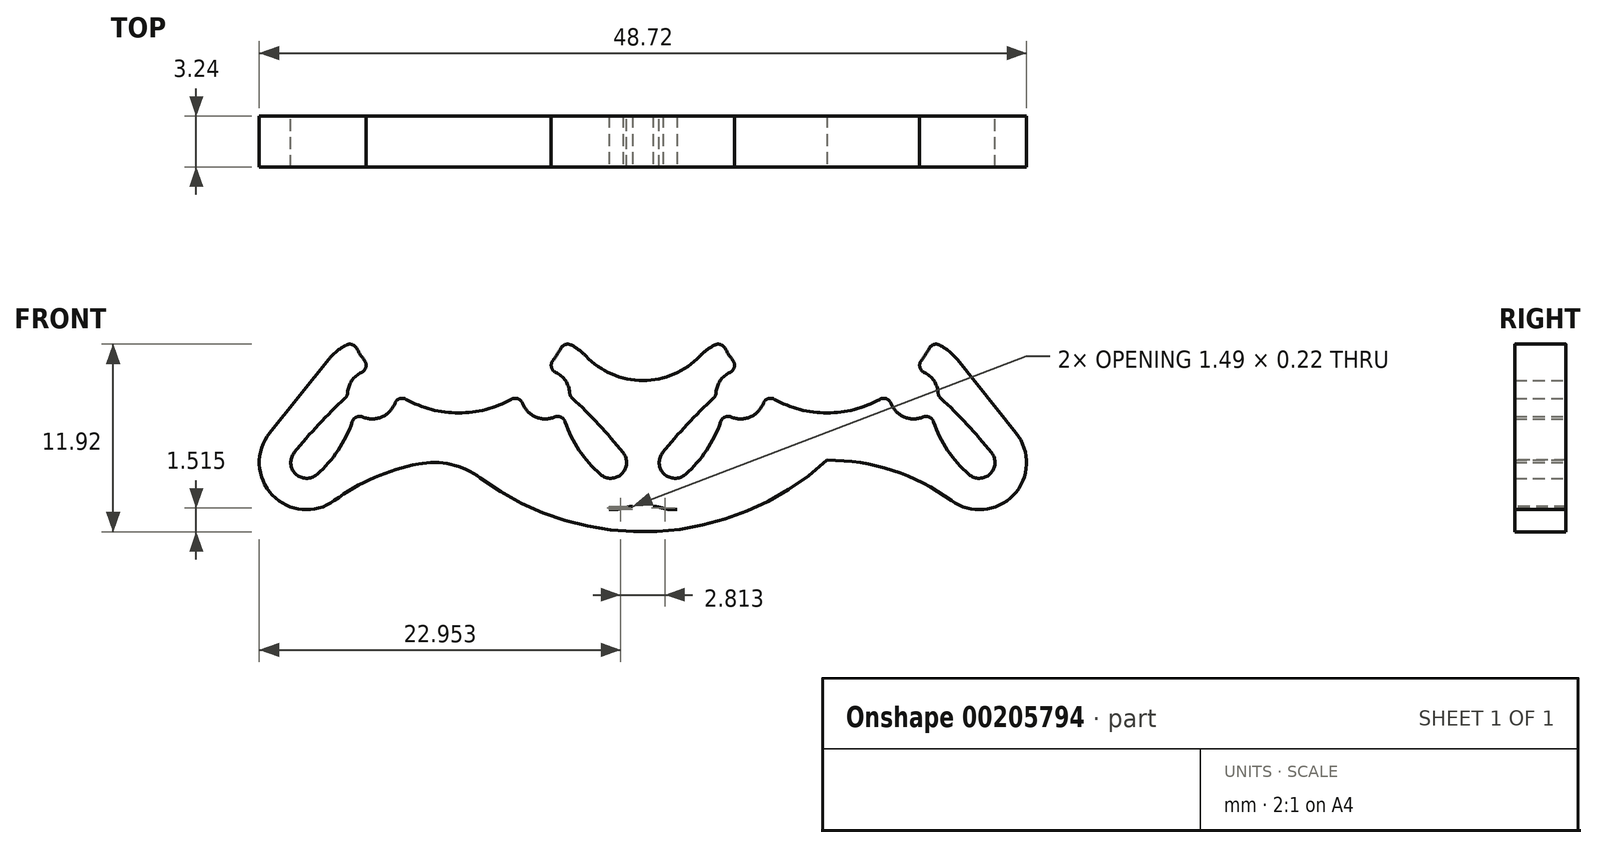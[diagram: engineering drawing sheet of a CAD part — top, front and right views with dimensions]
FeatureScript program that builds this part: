
annotation { "Feature Type Name" : "Feature", "Feature Type Description" : "" }
export const myFeature = defineFeature(function(context is Context, id is Id, definition is map)
    precondition{}
    {
        {
            var Q0;
            Q0=qCreatedBy(makeId("Front.planeOp"),FACE);
            var sketch = newSketch(context, id + "F0", { "sketchPlane" : qUnion([Q0])});
            skCircle(sketch, "E0", {"center": v(0, 0) * mm, "radius": 6.38 * mm});
            skPoint(sketch, "E1", {"position": v(0, 6.38) * mm});
            skPoint(sketch, "E2", {"position": v(0, 11.38) * mm});
            skCircle(sketch, "E3", {"center": v(-5.5, -5.7) * mm, "radius": 1.55 * mm});
            skLineSegment(sketch, "E4", {"start": v(0, 11.38) * mm, "end": v(0, 0) * mm, "construction": true});
            skCircle(sketch, "E5.MirrorC", {"center": v(5.5, -5.7) * mm, "radius": 1.55 * mm});
            skLineSegment(sketch, "E6", {"start": v(-5.5, -5.7) * mm, "end": v(5.5, -5.7) * mm, "construction": true});
            skSolve(sketch);
        }
        {
            var Q0;
            Q0=qCreatedBy(makeId("Front.planeOp"),FACE);
            var sketch = newSketch(context, id + "F1", { "sketchPlane" : qUnion([Q0])});
            skArc(sketch, "E7.0", {"start": v(-3.95, -5.63) * mm, "mid": v(-2.07, -6.56) * mm, "end": v(0, -6.88) * mm});
            skArc(sketch, "E8.3", {"start": v(-6.58, -6.82) * mm, "mid": v(-4.86, -7.12) * mm, "end": v(-3.95, -5.63) * mm});
            skLineSegment(sketch, "E9", {"start": v(0, 0) * mm, "end": v(-9.66, -10.03) * mm, "construction": true});
            skArc(sketch, "E10", {"start": v(-10.44, -9.4) * mm, "mid": v(-10.36, -10.75) * mm, "end": v(-9, -10.78) * mm});
            skLineSegment(sketch, "E11", {"start": v(-5.48, -4.16) * mm, "end": v(-7.05, -5.79) * mm, "construction": true});
            skLineSegment(sketch, "E12", {"start": v(-3.95, -5.63) * mm, "end": v(-5.52, -7.26) * mm, "construction": true});
            skLineSegment(sketch, "E13", {"start": v(-9, -10.78) * mm, "end": v(-4.74, -7.06) * mm, "construction": true});
            skPoint(sketch, "E13.endSnap0", {"position": v(-4.74, -6.44) * mm});
            skLineSegment(sketch, "E14", {"start": v(-6.7, -4.74) * mm, "end": v(-10.44, -9.4) * mm, "construction": true});
            skArc(sketch, "E15.trimOffspring", {"start": v(-12, -8.15) * mm, "mid": v(-11.83, -12.1) * mm, "end": v(-7.9, -12.45) * mm});
            skLineSegment(sketch, "E16", {"start": v(0, 0) * mm, "end": v(0, -9.88) * mm, "construction": true});
            skArc(sketch, "E17", {"start": v(0, -9.88) * mm, "mid": v(-4.15, -10.53) * mm, "end": v(-7.9, -12.45) * mm});
            skLineSegment(sketch, "E18", {"start": v(0, -9.88) * mm, "end": v(-5.5, -9.88) * mm, "construction": true});
            skLineSegment(sketch, "E19", {"start": v(0, -9.88) * mm, "end": v(0, -6.88) * mm});
            skArc(sketch, "E20", {"start": v(-5.48, -4.16) * mm, "mid": v(-6.62, -4.63) * mm, "end": v(-7.05, -5.79) * mm});
            skArc(sketch, "E21", {"start": v(-7.05, -5.79) * mm, "mid": v(-8.82, -7.53) * mm, "end": v(-10.44, -9.4) * mm});
            skLineSegment(sketch, "E22", {"start": v(-12, -8.15) * mm, "end": v(-8.27, -3.49) * mm});
            skArc(sketch, "E23", {"start": v(-6.7, -2.37) * mm, "mid": v(-6.16, -3.3) * mm, "end": v(-5.48, -4.16) * mm});
            skArc(sketch, "E24", {"start": v(-9, -10.78) * mm, "mid": v(-7.49, -8.99) * mm, "end": v(-6.58, -6.82) * mm});
            skLineSegment(sketch, "E25", {"start": v(-9.66, -13.03) * mm, "end": v(0, -13.03) * mm, "construction": true});
            skLineSegment(sketch, "E26", {"start": v(0, -13.03) * mm, "end": v(0, -6.88) * mm, "construction": true});
            skArc(sketch, "E27.trimOffspring", {"start": v(-6.7, -2.37) * mm, "mid": v(-7.56, -2.82) * mm, "end": v(-8.27, -3.49) * mm});
            skPoint(sketch, "E28.orphan", {"position": v(0, 8.37) * mm});
            skSolve(sketch);
        }
        {
            var Q0;
            Q0=qSketchRegion(id+"F1",true);
            extrude(context, id + "F2", {"entities" : qUnion([Q0]), "depth" : 3.25 * mm, "symmetric" : true});
        }
        {
            var Q0;
            Q0=makeQuery(id+"F2.opExtrude","SWEPT_EDGE",EDGE,{"disambiguationData":[OSD([sQuery(id+"F1.wireOp",EDGE,"E8.3"),sQuery(id+"F1.wireOp",EDGE,"f16a48b5-7a2a-4cbf-833e-9f4b7a7ec827.trimOffspring")])]});
            var Q1;
            Q1=makeQuery(id+"F2.opExtrude","SWEPT_EDGE",EDGE,{"disambiguationData":[OSD([sQuery(id+"F1.wireOp",EDGE,"0503ed2f-4905-41a0-8b90-6c5d83e06de4"),sQuery(id+"F1.wireOp",EDGE,"E8.3")])]});
            var Q2;
            Q2=makeQuery(id+"F2.opExtrude","SWEPT_EDGE",EDGE,{"disambiguationData":[OSD([sQuery(id+"F1.wireOp",EDGE,"E7.0"),sQuery(id+"F1.wireOp",EDGE,"E8.3")])]});
            var Q3;
            Q3=makeQuery(id+"F2.opExtrude","SWEPT_EDGE",EDGE,{"disambiguationData":[OSD([sQuery(id+"F1.wireOp",EDGE,"E20"),sQuery(id+"F1.wireOp",EDGE,"E21")])]});
            var Q4;
            Q4=makeQuery(id+"F2.opExtrude","SWEPT_EDGE",EDGE,{"disambiguationData":[OSD([sQuery(id+"F1.wireOp",EDGE,"E20"),sQuery(id+"F1.wireOp",EDGE,"aa0188ab-c223-4f96-b803-20454a8c8853")])]});
            var Q5;
            Q5=makeQuery(id+"F2.opExtrude","SWEPT_EDGE",EDGE,{"disambiguationData":[OSD([sQuery(id+"F1.wireOp",EDGE,"e83e305f-1027-4866-97f5-19716599f6f7"),sQuery(id+"F1.wireOp",EDGE,"E8.3")])]});
            var Q6;
            Q6=makeQuery(id+"F2.opExtrude","SWEPT_EDGE",EDGE,{"disambiguationData":[OSD([sQuery(id+"F1.wireOp",EDGE,"E10"),sQuery(id+"F1.wireOp",EDGE,"e83e305f-1027-4866-97f5-19716599f6f7")])]});
            var Q7;
            Q7=makeQuery(id+"F2.opExtrude","SWEPT_EDGE",EDGE,{"disambiguationData":[OSD([sQuery(id+"F1.wireOp",EDGE,"E23"),sQuery(id+"F1.wireOp",EDGE,"E27.trimOffspring")])]});
            fillet(context, id + "F3", {"entities" : qUnion([Q0, Q1, Q2, Q3, Q4, Q5, Q6, Q7]), "radius" : 0.5 * mm, "tangentPropagation" : true, "allowEdgeOverflow" : false});
        }
        {
            var Q0;
            Q0=makeQuery(id+"F2.opExtrude","SWEPT_BODY",BODY,{"disambiguationData":[OSD([sQuery(id+"F1.wireOp",EDGE,"91029bab-c422-4aac-b43c-f8eb8f7441cb.0"),sQuery(id+"F1.wireOp",EDGE,"E7.0"),sQuery(id+"F1.wireOp",EDGE,"E8.0"),sQuery(id+"F1.wireOp",EDGE,"E8.3"),sQuery(id+"F1.wireOp",EDGE,"4fe737ca-cd33-4ae7-bfb5-aca6cdd2fbdd"),sQuery(id+"F1.wireOp",EDGE,"E10"),sQuery(id+"F1.wireOp",EDGE,"87521696-a49b-46d6-ae6d-b95a5258b794"),sQuery(id+"F1.wireOp",EDGE,"3ad451f8-88f0-40d6-b978-8860d0f46c41"),sQuery(id+"F1.wireOp",EDGE,"RmzYGLSE-aIne-cmcq-fouj-xsO9WjanKBXf"),sQuery(id+"F1.wireOp",EDGE,"E1ndacnS-k5oY-T1jz-uEtG-vA6wWoizQWTL"),sQuery(id+"F1.wireOp",EDGE,"290a5299-caae-4b93-a680-34ceb27d99b0"),sQuery(id+"F1.wireOp",EDGE,"acf9eb55-ab42-4665-aab6-df971979b8c6"),sQuery(id+"F1.wireOp",EDGE,"0503ed2f-4905-41a0-8b90-6c5d83e06de4"),sQuery(id+"F1.wireOp",EDGE,"e83e305f-1027-4866-97f5-19716599f6f7"),sQuery(id+"F1.wireOp",EDGE,"E8.3"),sQuery(id+"F1.wireOp",EDGE,"E15.trimOffspring"),sQuery(id+"F1.wireOp",EDGE,"140a15c2-b3ae-4d8c-875c-2f7ce67bd9a0.trimOffspring"),sQuery(id+"F1.wireOp",EDGE,"f16a48b5-7a2a-4cbf-833e-9f4b7a7ec827.trimOffspring"),sQuery(id+"F1.wireOp",EDGE,"c726c67e-1b0a-4414-994c-10f8da0a7d9b.trimOffspring"),sQuery(id+"F1.wireOp",EDGE,"E17"),sQuery(id+"F1.wireOp",EDGE,"9d4cf9fb-cccf-4056-9c7a-a0118e21bfc9.trimOffspring"),sQuery(id+"F1.wireOp",EDGE,"aw0qZEzT-GYTq-v6Y8-Owwz-bXgHvjQE39bA"),sQuery(id+"F1.wireOp",EDGE,"E19"),sQuery(id+"F1.wireOp",EDGE,"e7ad43b5-d072-4a5a-872d-9ebe676b2ed9.trimOffspring")])]});
            var Q1;
            Q1=qCreatedBy(makeId("Right.planeOp"),FACE);
            mirror(context, id + "F4", {"operationType" : NewBodyOperationType.ADD, "entities" : qUnion([Q0]), "mirrorPlane" : qUnion([Q1])});
        }
        {
            var Q0;
            Q0=makeQuery(id+"F2.opExtrude","SWEPT_BODY",BODY,{"disambiguationData":[OSD([sQuery(id+"F1.wireOp",EDGE,"E7.0"),sQuery(id+"F1.wireOp",EDGE,"E10"),sQuery(id+"F1.wireOp",EDGE,"E8.3"),sQuery(id+"F1.wireOp",EDGE,"E15.trimOffspring"),sQuery(id+"F1.wireOp",EDGE,"E17"),sQuery(id+"F1.wireOp",EDGE,"E19"),sQuery(id+"F1.wireOp",EDGE,"E20"),sQuery(id+"F1.wireOp",EDGE,"E21"),sQuery(id+"F1.wireOp",EDGE,"E22"),sQuery(id+"F1.wireOp",EDGE,"E23"),sQuery(id+"F1.wireOp",EDGE,"E24"),sQuery(id+"F1.wireOp",EDGE,"E27.trimOffspring")])]});
            transform(context, id + "F5", {"entities" : qUnion([Q0]), "transformType" : TransformType.TRANSLATION_3D, "dx" : 23.4 * mm, "dy" : 0 * mm, "dz" : 0 * mm, "makeCopy" : true});
        }
        {
            var Q0;
            Q0=makeQuery(id+"F2.opExtrude","SWEPT_BODY",BODY,{"disambiguationData":[OSD([sQuery(id+"F1.wireOp",EDGE,"E7.0"),sQuery(id+"F1.wireOp",EDGE,"E10"),sQuery(id+"F1.wireOp",EDGE,"E8.3"),sQuery(id+"F1.wireOp",EDGE,"E15.trimOffspring"),sQuery(id+"F1.wireOp",EDGE,"E17"),sQuery(id+"F1.wireOp",EDGE,"E19"),sQuery(id+"F1.wireOp",EDGE,"E20"),sQuery(id+"F1.wireOp",EDGE,"E21"),sQuery(id+"F1.wireOp",EDGE,"E22"),sQuery(id+"F1.wireOp",EDGE,"E23"),sQuery(id+"F1.wireOp",EDGE,"E24"),sQuery(id+"F1.wireOp",EDGE,"E27.trimOffspring")])]});
            var Q1;
            Q1=makeQuery(id+"F5.opPattern","COPY",BODY,{"derivedFrom":makeQuery(id+"F2.opExtrude","SWEPT_BODY",BODY,{"disambiguationData":[OSD([sQuery(id+"F1.wireOp",EDGE,"E7.0"),sQuery(id+"F1.wireOp",EDGE,"E10"),sQuery(id+"F1.wireOp",EDGE,"E8.3"),sQuery(id+"F1.wireOp",EDGE,"E15.trimOffspring"),sQuery(id+"F1.wireOp",EDGE,"E17"),sQuery(id+"F1.wireOp",EDGE,"E19"),sQuery(id+"F1.wireOp",EDGE,"E20"),sQuery(id+"F1.wireOp",EDGE,"E21"),sQuery(id+"F1.wireOp",EDGE,"E22"),sQuery(id+"F1.wireOp",EDGE,"E23"),sQuery(id+"F1.wireOp",EDGE,"E24"),sQuery(id+"F1.wireOp",EDGE,"E27.trimOffspring")])]}),"instanceName":"1"});
            booleanBodies(context, id + "F6", {"operationType" : BooleanOperationType.UNION, "tools" : qUnion([Q0, Q1])});
        }
        {
            var Q0;
            {var subQ0=makeQuery(id+"F2.opExtrude","SWEPT_FACE",FACE,{"disambiguationData":[OSD([sQuery(id+"F1.wireOp",EDGE,"E22")])]});Q0=makeQuery(id+"F6.opBoolean","INTERSECT",EDGE,{"derivedFrom":[makeQuery(id+"F4.opPattern","COPY",FACE,{"derivedFrom":subQ0,"instanceName":"1"}),makeQuery(id+"F5.opPattern","COPY",FACE,{"derivedFrom":subQ0,"instanceName":"1"})]});}
            var Q1;
            {var subQ0=makeQuery(id+"F2.opExtrude","SWEPT_FACE",FACE,{"disambiguationData":[OSD([sQuery(id+"F1.wireOp",EDGE,"E15.trimOffspring")])]});Q1=makeQuery(id+"F6.opBoolean","INTERSECT",EDGE,{"derivedFrom":[makeQuery(id+"F4.opPattern","COPY",FACE,{"derivedFrom":subQ0,"instanceName":"1"}),makeQuery(id+"F5.opPattern","COPY",FACE,{"derivedFrom":subQ0,"instanceName":"1"})]});}
            fillet(context, id + "F7", {"entities" : qUnion([Q0, Q1]), "radius" : 5 * mm, "tangentPropagation" : true, "allowEdgeOverflow" : false});
        }
        {
            var Q0;
            Q0=qCreatedBy(makeId("Front.planeOp"),FACE);
            var sketch = newSketch(context, id + "F8", { "sketchPlane" : qUnion([Q0])});
            skArc(sketch, "E29", {"start": v(0, -9.88) * mm, "mid": v(11.7, -14.43) * mm, "end": v(23.4, -9.87) * mm});
            skLineSegment(sketch, "E30", {"start": v(11.7, -4.82) * mm, "end": v(11.7, -14.43) * mm, "construction": true});
            skArc(sketch, "E31.0", {"start": v(7.9, -12.45) * mm, "mid": v(4.15, -10.53) * mm, "end": v(0, -9.88) * mm});
            skArc(sketch, "E31.1", {"start": v(10.43, -12.93) * mm, "mid": v(9.1, -12.97) * mm, "end": v(7.9, -12.45) * mm});
            skArc(sketch, "E31.2", {"start": v(10.43, -12.93) * mm, "mid": v(11.7, -12.76) * mm, "end": v(12.97, -12.93) * mm});
            skArc(sketch, "E31.3", {"start": v(12.97, -12.93) * mm, "mid": v(14.3, -12.97) * mm, "end": v(15.5, -12.45) * mm});
            skArc(sketch, "E32.0", {"start": v(23.4, -9.88) * mm, "mid": v(19.25, -10.53) * mm, "end": v(15.5, -12.45) * mm});
            skSolve(sketch);
        }
        {
            var Q0;
            Q0=makeQuery(id+"F8.imprint","IMPRINT",FACE,{"disambiguationData":[TD([[makeQuery(id+"F8.imprint","IMPRINT",EDGE,{"derivedFrom":sQuery(id+"F8.wireOp",EDGE,"E29")}),1.0]])]});
            var Q1;
            {var subQ0=makeQuery(id+"F2.opExtrude","CAP_FACE",FACE,{"disambiguationData":[OSD([sQuery(id+"F1.wireOp",EDGE,"E7.0"),sQuery(id+"F1.wireOp",EDGE,"E10"),sQuery(id+"F1.wireOp",EDGE,"E8.3"),sQuery(id+"F1.wireOp",EDGE,"E15.trimOffspring"),sQuery(id+"F1.wireOp",EDGE,"E17"),sQuery(id+"F1.wireOp",EDGE,"E19"),sQuery(id+"F1.wireOp",EDGE,"E20"),sQuery(id+"F1.wireOp",EDGE,"E21"),sQuery(id+"F1.wireOp",EDGE,"E22"),sQuery(id+"F1.wireOp",EDGE,"E23"),sQuery(id+"F1.wireOp",EDGE,"E24"),sQuery(id+"F1.wireOp",EDGE,"E27.trimOffspring")])],"isStart":true});var subQ1=makeQuery(id+"F4.boolean.opBoolean","MERGE",FACE,{"derivedFrom":[subQ0,makeQuery(id+"F4.opPattern","COPY",FACE,{"derivedFrom":subQ0,"instanceName":"1"})]});Q1=makeQuery(id+"F6.opBoolean","MERGE",FACE,{"derivedFrom":[subQ1,makeQuery(id+"F5.opPattern","COPY",FACE,{"derivedFrom":subQ1,"instanceName":"1"})]});}
            extrude(context, id + "F9", {"entities" : qUnion([Q0]), "operationType" : NewBodyOperationType.ADD, "oppositeDirection" : true, "endBoundEntityFace" : qUnion([Q1]), "depth" : 3.25 * mm, "hasSecondDirection" : true, "secondDirectionBound" : BoundingType.UP_TO_SURFACE, "secondDirectionOppositeDirection" : true, "secondDirectionDepth" : 25 * mm, "symmetric" : true});
        }
        {
            var Q0;
            Q0=makeQuery(id+"F9.opExtrude","SWEPT_EDGE",EDGE,{"disambiguationData":[OSD([sQuery(id+"F8.wireOp",EDGE,"E29"),sQuery(id+"F8.wireOp",EDGE,"E32.0")])]});
            var Q1;
            Q1=makeQuery(id+"F9.opExtrude","SWEPT_EDGE",EDGE,{"disambiguationData":[OSD([sQuery(id+"F8.wireOp",EDGE,"E29"),sQuery(id+"F8.wireOp",EDGE,"E31.0")])]});
            fillet(context, id + "F10", {"entities" : qUnion([Q0, Q1]), "radius" : 5 * mm, "tangentPropagation" : true, "allowEdgeOverflow" : false});
        }
    });
